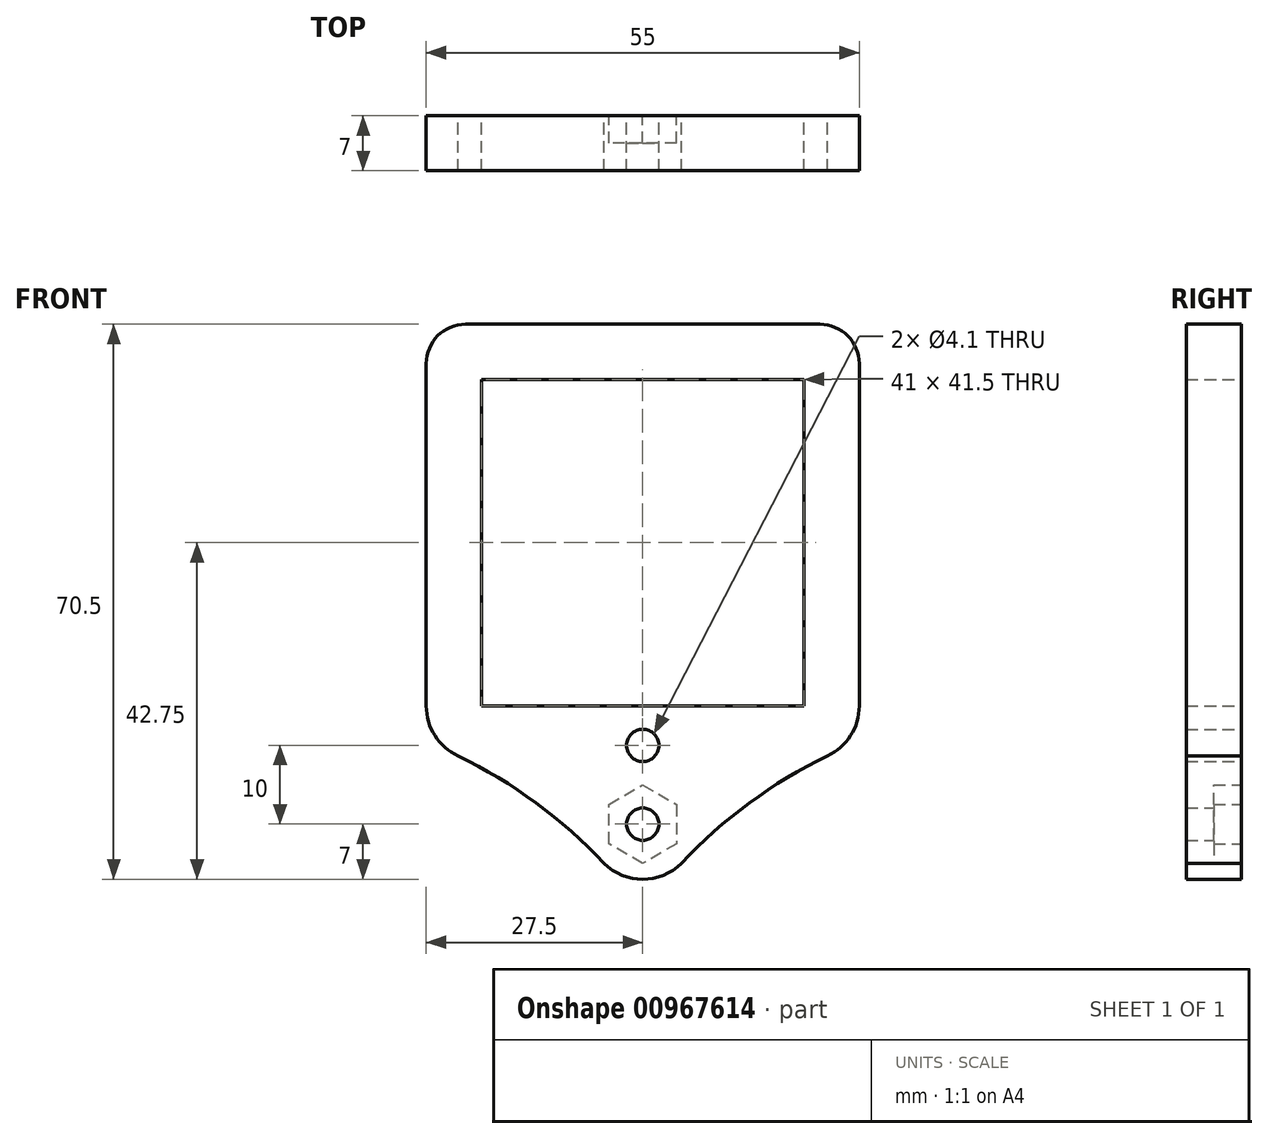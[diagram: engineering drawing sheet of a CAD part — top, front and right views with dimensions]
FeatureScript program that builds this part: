
annotation { "Feature Type Name" : "Feature", "Feature Type Description" : "" }
export const myFeature = defineFeature(function(context is Context, id is Id, definition is map)
    precondition{}
    {
        {
            var Q0;
            Q0=qCreatedBy(makeId("Front.planeOp"),FACE);
            var sketch = newSketch(context, id + "F0", { "sketchPlane" : qUnion([Q0])});
            skLineSegment(sketch, "E0.bottom", {"start": v(20.5, 20.75) * mm, "end": v(-20.5, 20.75) * mm});
            skLineSegment(sketch, "E0.top", {"start": v(20.5, -20.75) * mm, "end": v(-20.5, -20.75) * mm});
            skLineSegment(sketch, "E0.left", {"start": v(20.5, 20.75) * mm, "end": v(20.5, -20.75) * mm});
            skLineSegment(sketch, "E0.right", {"start": v(-20.5, 20.75) * mm, "end": v(-20.5, -20.75) * mm});
            skPoint(sketch, "E0.middle", {"position": v(0, 0) * mm});
            skPoint(sketch, "E1", {"position": v(0, -20.75) * mm});
            skArc(sketch, "E2", {"start": v(-4.91, -40.73) * mm, "mid": v(0, -42.75) * mm, "end": v(4.91, -40.73) * mm});
            skCircle(sketch, "E3.cCircle", {"center": v(0, -35.75) * mm, "radius": 4.97 * mm, "construction": true});
            skLineSegment(sketch, "E3.0", {"start": v(4.3, -38.24) * mm, "end": v(0, -40.73) * mm});
            skLineSegment(sketch, "E3.1", {"start": v(0, -40.73) * mm, "end": v(-4.3, -38.24) * mm});
            skLineSegment(sketch, "E3.2", {"start": v(-4.3, -38.24) * mm, "end": v(-4.3, -33.26) * mm});
            skLineSegment(sketch, "E3.3", {"start": v(-4.3, -33.26) * mm, "end": v(0, -30.78) * mm});
            skLineSegment(sketch, "E3.4", {"start": v(0, -30.78) * mm, "end": v(4.3, -33.26) * mm});
            skLineSegment(sketch, "E3.5", {"start": v(4.3, -33.26) * mm, "end": v(4.3, -38.24) * mm});
            skCircle(sketch, "E4", {"center": v(0, -35.75) * mm, "radius": 2.05 * mm});
            skLineSegment(sketch, "E5.0", {"start": v(-27.5, 22.75) * mm, "end": v(-27.5, -20.75) * mm});
            skLineSegment(sketch, "E6.0", {"start": v(22.5, 27.75) * mm, "end": v(-22.5, 27.75) * mm});
            skLineSegment(sketch, "E7.0", {"start": v(27.5, 22.75) * mm, "end": v(27.5, -20.75) * mm});
            skArc(sketch, "E8.filletArc", {"start": v(-22.5, 27.75) * mm, "mid": v(-26.04, 26.29) * mm, "end": v(-27.5, 22.75) * mm});
            skArc(sketch, "E9.filletArc", {"start": v(27.5, 22.75) * mm, "mid": v(26.04, 26.29) * mm, "end": v(22.5, 27.75) * mm});
            skArc(sketch, "E10", {"start": v(23.47, -27.09) * mm, "mid": v(26.4, -24.5) * mm, "end": v(27.5, -20.75) * mm});
            skCircle(sketch, "E11", {"center": v(0, -25.75) * mm, "radius": 2.05 * mm});
            skArc(sketch, "E12", {"start": v(23.47, -27.09) * mm, "mid": v(13.56, -33.05) * mm, "end": v(4.91, -40.73) * mm});
            skPoint(sketch, "E12.third.point", {"position": v(108.3, -58.65) * mm});
            skArc(sketch, "E13.MirrorCS", {"start": v(-23.47, -27.09) * mm, "mid": v(-13.56, -33.05) * mm, "end": v(-4.91, -40.73) * mm});
            skArc(sketch, "E14.MirrorCS", {"start": v(-23.47, -27.09) * mm, "mid": v(-26.4, -24.5) * mm, "end": v(-27.5, -20.75) * mm});
            skSolve(sketch);
        }
        {
            var Q0;
            Q0=makeQuery(id+"F0.imprint","IMPRINT",FACE,{"disambiguationData":[TD([[makeQuery(id+"F0.imprint","IMPRINT",EDGE,{"derivedFrom":sQuery(id+"F0.wireOp",EDGE,"E0.bottom")}),-1.0]])]});
            extrude(context, id + "F1", {"entities" : qUnion([Q0]), "endBound" : BoundingType.SYMMETRIC, "depth" : 7 * mm, "offsetDistance" : 25 * mm});
        }
        {
            var Q0;
            Q0=makeQuery(id+"F0.imprint","IMPRINT",FACE,{"disambiguationData":[TD([[makeQuery(id+"F0.imprint","IMPRINT",EDGE,{"derivedFrom":sQuery(id+"F0.wireOp",EDGE,"E3.0")}),-1.0]])]});
            extrude(context, id + "F2", {"entities" : qUnion([Q0]), "operationType" : NewBodyOperationType.ADD, "depth" : 3.5 * mm, "offsetDistance" : 25 * mm});
        }
    });
